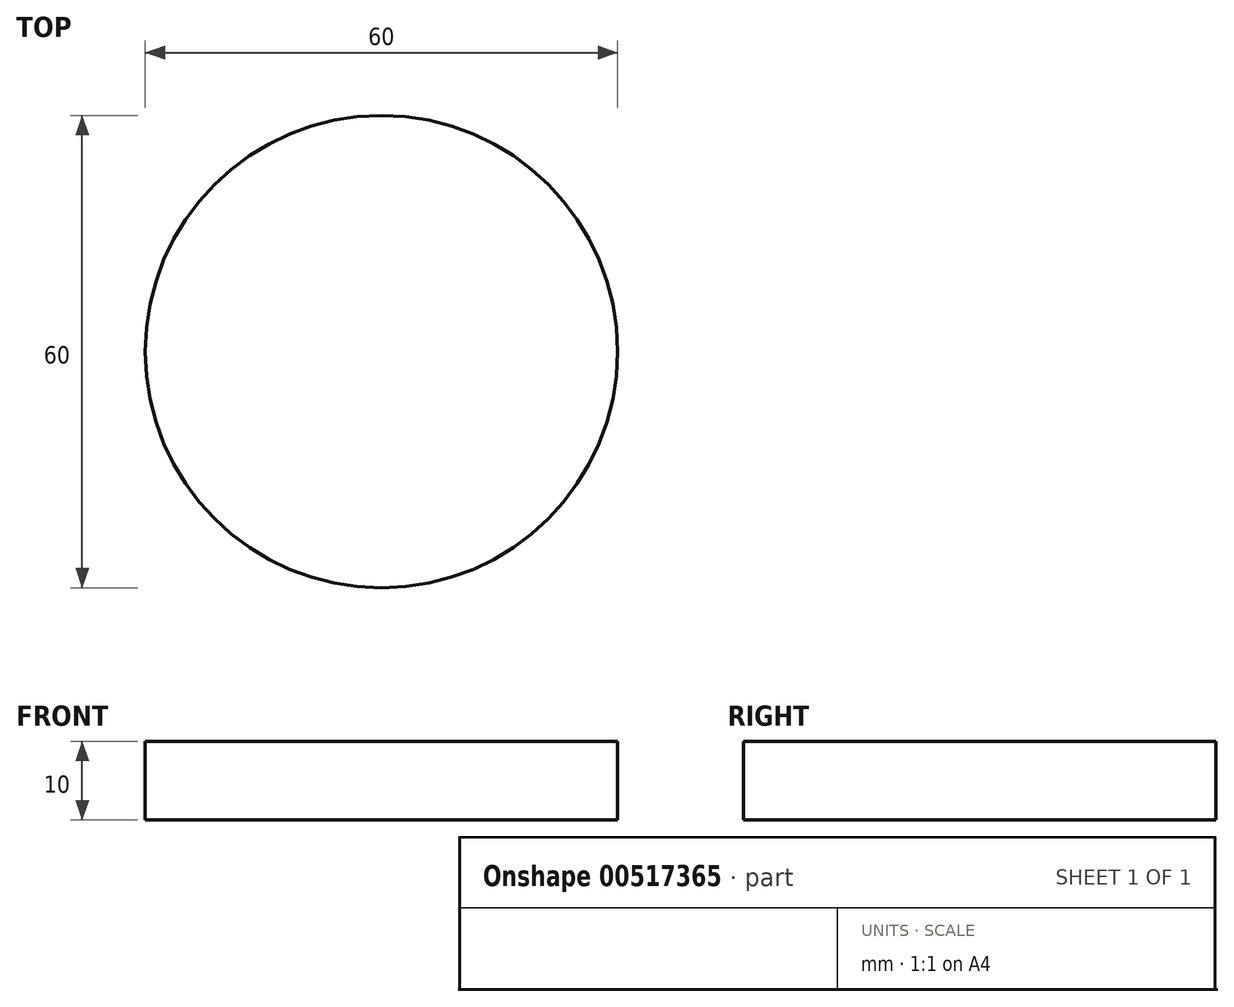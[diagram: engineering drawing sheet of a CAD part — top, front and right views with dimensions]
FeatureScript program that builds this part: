
annotation { "Feature Type Name" : "Feature", "Feature Type Description" : "" }
export const myFeature = defineFeature(function(context is Context, id is Id, definition is map)
    precondition{}
    {
        {
            var Q0;
            Q0=qCreatedBy(makeId("Top.planeOp"),FACE);
            var sketch = newSketch(context, id + "F0", { "sketchPlane" : qUnion([Q0])});
            skCircle(sketch, "E0", {"center": v(0, 0) * mm, "radius": 30 * mm});
            skSolve(sketch);
        }
        {
            var Q0;
            Q0=makeQuery(id+"F0.imprint","IMPRINT",FACE,{"disambiguationData":[TD([[makeQuery(id+"F0.imprint","IMPRINT",EDGE,{"derivedFrom":sQuery(id+"F0.wireOp",EDGE,"E0")}),1.0]])]});
            extrude(context, id + "F1", {"entities" : qUnion([Q0]), "depth" : 10 * mm, "offsetDistance" : 25 * mm});
        }
    });
